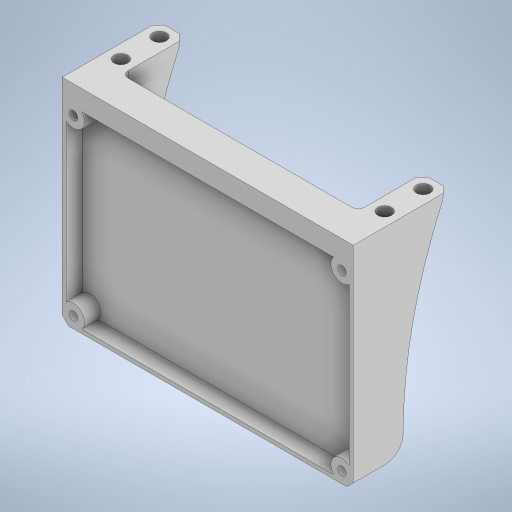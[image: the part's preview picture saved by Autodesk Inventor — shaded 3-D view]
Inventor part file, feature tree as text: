
AUTODESK INVENTOR PART (.ipt)
format: ipt  version: 2023 (Build 270158000, 158)  size: 392,704 bytes
history: native  units: mm
features: extrude x5, sketch x5, chamfer x2, projected_geometry x2, pattern_linear x1, fillet x1
ambient origin geometry x8: Origin, YZ Plane, XZ Plane, XY Plane, X Axis, Y Axis, Z Axis, Center Point
bodies: Solid1 (feature_tree)
feature tree (16):
  extrude  "Extrusion1"  Depth=83.5mm
  extrude  "Extrusion2"  Depth=61.0mm
  extrude  "Extrusion3"  Depth=5.0mm TaperAngle=0.0deg
  extrude  "Extrusion4"  Depth=5.0mm TaperAngle=0.0deg
  pattern_linear  "Rectangular Pattern1"  Count1=2  [1 undecoded]
  fillet  "Fillet2"  Radius=135.0mm
  extrude  "Extrusion5"  Depth=10.0mm
  chamfer  "Chamfer1"  Distance=8.5mm
  chamfer  "Chamfer2"  Distance=1.25mm
  sketch  "Sketch1"  dims[d0=54.0mm d1=83.5mm]
  sketch  "Sketch2"  dims[d2=90.5mm d3=61.0mm]
  sketch  "Sketch3"  dims[d4=2.7mm d5=5.0mm d6=0.0mm]
  projected_geometry  "Projected Loop2"
  sketch  "Sketch4"  dims[d8=7.0mm d12=5.0mm d13=0.0mm]
  sketch  "Sketch5"  dims[d16=90.0deg d17=20.0mm d18=135.0mm d19=7.5mm d20=8.5mm d21=0.0mm d22=1.25mm d23=1.25mm d24=20.0mm d26=82.0mm d27=5.0mm d28=4.318mm d29=12.0mm d30=50.25mm d31=0.0mm d32=2.0mm d33=10.0mm d34=8.5mm d35=0.0mm d36=2.0mm d37=2.0mm d38=45.0deg d39=2.0mm d40=2.0mm d41=45.0deg]
  projected_geometry  "Projected Loop3"
note: 1 required parameter value undecoded (feature->parameter linkage not recoverable at this tier; creation-order binding heuristic only, values carry confidence <= 0.55)
